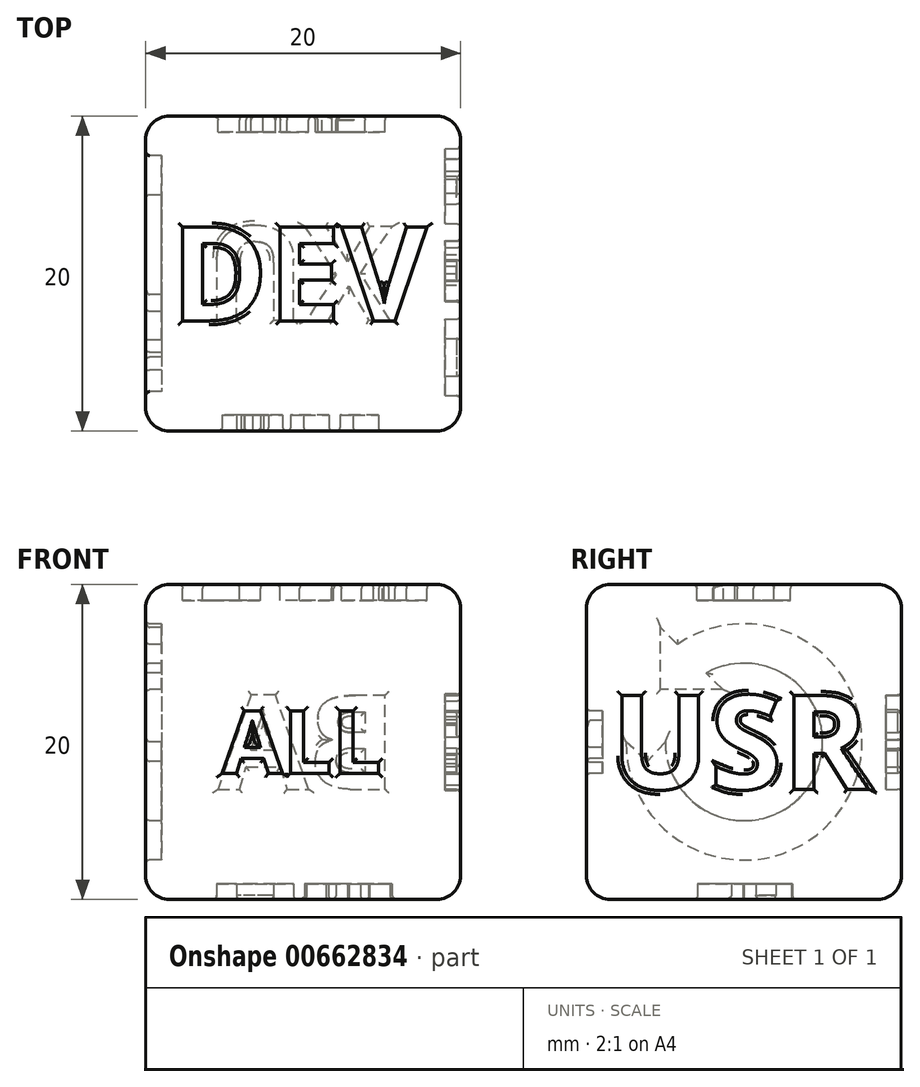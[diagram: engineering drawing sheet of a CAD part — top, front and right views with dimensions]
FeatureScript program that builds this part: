
annotation { "Feature Type Name" : "Feature", "Feature Type Description" : "" }
export const myFeature = defineFeature(function(context is Context, id is Id, definition is map)
    precondition{}
    {
        {
            assignVariable(context, id + "F0", {"name" : "textDepth", "anyValue" : 1});
        }
        {
            var Q0;
            Q0=qCreatedBy(makeId("Top.planeOp"),FACE);
            var sketch = newSketch(context, id + "F1", { "sketchPlane" : qUnion([Q0])});
            skLineSegment(sketch, "E0.bottom", {"start": v(0, 0) * mm, "end": v(20, 0) * mm});
            skLineSegment(sketch, "E0.top", {"start": v(0, 20) * mm, "end": v(20, 20) * mm});
            skLineSegment(sketch, "E0.left", {"start": v(0, 0) * mm, "end": v(0, 20) * mm});
            skLineSegment(sketch, "E0.right", {"start": v(20, 0) * mm, "end": v(20, 20) * mm});
            skSolve(sketch);
        }
        {
            var Q0;
            Q0 = qSketchRegion(id + "F1", true);
            extrude(context, id + "F2", {"entities" : qUnion([Q0]), "depth" : 20 * mm, "offsetDistance" : 25 * mm});
        }
        {
            var Q0;
            Q0=makeQuery(id+"F2.opExtrude","CAP_FACE",FACE,{"disambiguationData":[OSD([sQuery(id+"F1.wireOp",EDGE,"E0.bottom"),sQuery(id+"F1.wireOp",EDGE,"E0.top"),sQuery(id+"F1.wireOp",EDGE,"E0.left"),sQuery(id+"F1.wireOp",EDGE,"E0.right")])],"isStart":false});
            var Q1;
            Q1=makeQuery(id+"F2.opExtrude","SWEPT_FACE",FACE,{"disambiguationData":[OSD([sQuery(id+"F1.wireOp",EDGE,"E0.right")])]});
            var Q2;
            Q2=makeQuery(id+"F2.opExtrude","SWEPT_FACE",FACE,{"disambiguationData":[OSD([sQuery(id+"F1.wireOp",EDGE,"E0.bottom")])]});
            var Q3;
            Q3=makeQuery(id+"F2.opExtrude","CAP_FACE",FACE,{"disambiguationData":[OSD([sQuery(id+"F1.wireOp",EDGE,"E0.bottom"),sQuery(id+"F1.wireOp",EDGE,"E0.top"),sQuery(id+"F1.wireOp",EDGE,"E0.left"),sQuery(id+"F1.wireOp",EDGE,"E0.right")])],"isStart":true});
            var Q4;
            Q4=makeQuery(id+"F2.opExtrude","SWEPT_FACE",FACE,{"disambiguationData":[OSD([sQuery(id+"F1.wireOp",EDGE,"E0.top")])]});
            var Q5;
            Q5=makeQuery(id+"F2.opExtrude","SWEPT_FACE",FACE,{"disambiguationData":[OSD([sQuery(id+"F1.wireOp",EDGE,"E0.left")])]});
            fillet(context, id + "F3", {"entities" : qUnion([Q0, Q1, Q2, Q3, Q4, Q5]), "radius" : 1.5 * mm, "tangentPropagation" : true, "allowEdgeOverflow" : false});
        }
        {
            var Q0;
            Q0=makeQuery(id+"F2.opExtrude","CAP_FACE",FACE,{"disambiguationData":[OSD([sQuery(id+"F1.wireOp",EDGE,"E0.bottom"),sQuery(id+"F1.wireOp",EDGE,"E0.top"),sQuery(id+"F1.wireOp",EDGE,"E0.left"),sQuery(id+"F1.wireOp",EDGE,"E0.right")])],"isStart":false});
            var sketch = newSketch(context, id + "F4", { "sketchPlane" : qUnion([Q0])});
            skText(sketch, "E1", { "text": "DEV", "fontName": "OpenSans-Bold.ttf"});
            skLineSegment(sketch, "E2", {"start": v(10, 18.5) * mm, "end": v(10, 1.5) * mm, "construction": true});
            skLineSegment(sketch, "E3", {"start": v(1.6, 10) * mm, "end": v(18.4, 10) * mm, "construction": true});
            skLineSegment(sketch, "E4", {"start": v(1.5, 10) * mm, "end": v(18.5, 10) * mm, "construction": true});
            const initialGuessF4  = {"E1": [0.0016, 0.007, 1, 0, 0.006]};
            skSetInitialGuess(sketch, initialGuessF4);
            skSolve(sketch);
        }
        {
            var Q0;
            Q0 = qSketchRegion(id + "F4", true);
            extrude(context, id + "F5", {"entities" : qUnion([Q0]), "operationType" : NewBodyOperationType.REMOVE, "oppositeDirection" : true, "depth" : (getVariable(context, 'textDepth')) * mm, "offsetDistance" : 25 * mm});
        }
        {
            var Q0;
            Q0=makeQuery(id+"F2.opExtrude","SWEPT_FACE",FACE,{"disambiguationData":[OSD([sQuery(id+"F1.wireOp",EDGE,"E0.bottom")])]});
            var sketch = newSketch(context, id + "F6", { "sketchPlane" : qUnion([Q0])});
            skLineSegment(sketch, "E5", {"start": v(1.5, 10) * mm, "end": v(18.5, 10) * mm, "construction": true});
            skLineSegment(sketch, "E6", {"start": v(10, 18.5) * mm, "end": v(10, 1.5) * mm, "construction": true});
            skText(sketch, "E7", { "text": "ALL", "fontName": "OpenSans-Bold.ttf"});
            skLineSegment(sketch, "E8", {"start": v(2.29, 10) * mm, "end": v(17.71, 10) * mm, "construction": true});
            const initialGuessF6  = {"E7": [0.00486, 0.008, 1, 0, 0.004]};
            skSetInitialGuess(sketch, initialGuessF6);
            skSolve(sketch);
        }
        {
            var Q0;
            Q0 = qSketchRegion(id + "F6", true);
            extrude(context, id + "F7", {"entities" : qUnion([Q0]), "operationType" : NewBodyOperationType.REMOVE, "oppositeDirection" : true, "depth" : (getVariable(context, 'textDepth')) * mm, "offsetDistance" : 25 * mm});
        }
        {
            var Q0;
            Q0=makeQuery(id+"F2.opExtrude","SWEPT_FACE",FACE,{"disambiguationData":[OSD([sQuery(id+"F1.wireOp",EDGE,"E0.right")])]});
            var sketch = newSketch(context, id + "F8", { "sketchPlane" : qUnion([Q0])});
            skLineSegment(sketch, "E9", {"start": v(1.5, 10) * mm, "end": v(18.5, 10) * mm, "construction": true});
            skLineSegment(sketch, "E10", {"start": v(10, 18.5) * mm, "end": v(10, 1.5) * mm, "construction": true});
            skText(sketch, "E11", { "text": "USR", "fontName": "OpenSans-Bold.ttf"});
            skLineSegment(sketch, "E12", {"start": v(1.53, 10) * mm, "end": v(18.47, 10) * mm, "construction": true});
            const initialGuessF8  = {"E11": [0.00153, 0.007, 1, 0, 0.006]};
            skSetInitialGuess(sketch, initialGuessF8);
            skSolve(sketch);
        }
        {
            var Q0;
            Q0 = qSketchRegion(id + "F8", true);
            extrude(context, id + "F9", {"entities" : qUnion([Q0]), "operationType" : NewBodyOperationType.REMOVE, "oppositeDirection" : true, "depth" : (getVariable(context, 'textDepth')) * mm, "offsetDistance" : 25 * mm});
        }
        {
            var Q0;
            Q0=makeQuery(id+"F2.opExtrude","SWEPT_FACE",FACE,{"disambiguationData":[OSD([sQuery(id+"F1.wireOp",EDGE,"E0.top")])]});
            var sketch = newSketch(context, id + "F10", { "sketchPlane" : qUnion([Q0])});
            skLineSegment(sketch, "E13", {"start": v(-18.5, 10) * mm, "end": v(-1.5, 10) * mm, "construction": true});
            skLineSegment(sketch, "E14", {"start": v(-10, 18.5) * mm, "end": v(-10, 1.5) * mm, "construction": true});
            skText(sketch, "E15", { "text": "BA", "fontName": "OpenSans-Bold.ttf"});
            skLineSegment(sketch, "E16", {"start": v(-15.94, 10) * mm, "end": v(-4.06, 10) * mm, "construction": true});
            const initialGuessF10  = {"E15": [-0.01594, 0.007, 1, 0, 0.006]};
            skSetInitialGuess(sketch, initialGuessF10);
            skSolve(sketch);
        }
        {
            var Q0;
            Q0 = qSketchRegion(id + "F10", true);
            extrude(context, id + "F11", {"entities" : qUnion([Q0]), "operationType" : NewBodyOperationType.REMOVE, "oppositeDirection" : true, "depth" : (getVariable(context, 'textDepth')) * mm, "offsetDistance" : 25 * mm});
        }
        {
            var Q0;
            Q0=makeQuery(id+"F2.opExtrude","CAP_FACE",FACE,{"disambiguationData":[OSD([sQuery(id+"F1.wireOp",EDGE,"E0.bottom"),sQuery(id+"F1.wireOp",EDGE,"E0.top"),sQuery(id+"F1.wireOp",EDGE,"E0.left"),sQuery(id+"F1.wireOp",EDGE,"E0.right")])],"isStart":true});
            var sketch = newSketch(context, id + "F12", { "sketchPlane" : qUnion([Q0])});
            skLineSegment(sketch, "E17", {"start": v(18.5, -10) * mm, "end": v(1.5, -10) * mm, "construction": true});
            skLineSegment(sketch, "E18", {"start": v(10, -18.5) * mm, "end": v(10, -1.5) * mm, "construction": true});
            skText(sketch, "E19", { "text": "UX", "fontName": "OpenSans-Bold.ttf"});
            skLineSegment(sketch, "E20", {"start": v(16.2, -10) * mm, "end": v(3.8, -10) * mm, "construction": true});
            const initialGuessF12  = {"E19": [0.0038, -0.013, 1, 0, 0.006]};
            skSetInitialGuess(sketch, initialGuessF12);
            skSolve(sketch);
        }
        {
            var Q0;
            Q0 = qSketchRegion(id + "F12", true);
            extrude(context, id + "F13", {"entities" : qUnion([Q0]), "operationType" : NewBodyOperationType.REMOVE, "oppositeDirection" : true, "depth" : (getVariable(context, 'textDepth')) * mm, "offsetDistance" : 25 * mm});
        }
        {
            var Q0;
            Q0=makeQuery(id+"F2.opExtrude","SWEPT_FACE",FACE,{"disambiguationData":[OSD([sQuery(id+"F1.wireOp",EDGE,"E0.left")])]});
            var sketch = newSketch(context, id + "F14", { "sketchPlane" : qUnion([Q0])});
            skLineSegment(sketch, "E21", {"start": v(-18.5, 10) * mm, "end": v(-1.5, 10) * mm, "construction": true});
            skLineSegment(sketch, "E22", {"start": v(-10, 18.5) * mm, "end": v(-10, 1.5) * mm, "construction": true});
            skArc(sketch, "E23", {"start": v(-5.78, 16.2) * mm, "mid": v(-16.63, 6.5) * mm, "end": v(-2.5, 10) * mm});
            skArc(sketch, "E24", {"start": v(-7.6, 14.38) * mm, "mid": v(-14.3, 7.45) * mm, "end": v(-5, 10) * mm});
            skLineSegment(sketch, "E25", {"start": v(-8.65, 13.32) * mm, "end": v(-7.6, 14.38) * mm});
            skLineSegment(sketch, "E26", {"start": v(-8.65, 13.32) * mm, "end": v(-4.7, 13.32) * mm});
            skLineSegment(sketch, "E27", {"start": v(-4.7, 13.32) * mm, "end": v(-4.7, 17.27) * mm});
            skCircle(sketch, "E28", {"center": v(-10, 10) * mm, "radius": 6.25 * mm, "construction": true});
            skLineSegment(sketch, "E29", {"start": v(-4.7, 13.32) * mm, "end": v(-6.68, 15.3) * mm, "construction": true});
            skLineSegment(sketch, "E30", {"start": v(-10, 10) * mm, "end": v(-1.5, 18.5) * mm, "construction": true});
            skLineSegment(sketch, "E31", {"start": v(-5, 10) * mm, "end": v(-3.87, 8.77) * mm});
            skLineSegment(sketch, "E32", {"start": v(-3.87, 8.77) * mm, "end": v(-2.5, 10) * mm});
            skArc(sketch, "E33.trimOffspring", {"start": v(-4.7, 15.3) * mm, "mid": v(-4.7, 15.3) * mm, "end": v(-4.7, 15.31) * mm});
            skLineSegment(sketch, "E34.trimOffspring", {"start": v(-5.78, 16.2) * mm, "end": v(-4.7, 17.27) * mm});
            skSolve(sketch);
        }
        {
            var Q0;
            Q0 = qSketchRegion(id + "F14", true);
            extrude(context, id + "F15", {"entities" : qUnion([Q0]), "operationType" : NewBodyOperationType.REMOVE, "oppositeDirection" : true, "depth" : (getVariable(context, 'textDepth')) * mm, "offsetDistance" : 25 * mm});
        }
        {
            var Q0;
            Q0=makeQuery(id+"F2.opExtrude","SWEPT_FACE",FACE,{"disambiguationData":[OSD([sQuery(id+"F1.wireOp",EDGE,"E0.left")])]});
            var Q1;
            {var subQ1=sQuery(id+"F1.wireOp",EDGE,"E0.bottom");Q1=makeQuery(id+"F7.boolean.opBoolean","SPLIT",FACE,{"disambiguationData":[TD([makeQuery(id+"F7.opExtrude","SWEPT_FACE",FACE,{"disambiguationData":[OSD([sQuery(id+"F6.wireOp",EDGE,"E7.sketch_text.stroke-0")])]})])],"derivedFrom":makeQuery(id+"F2.opExtrude","SWEPT_FACE",FACE,{"disambiguationData":[OSD([subQ1])]})});}
            var Q2;
            Q2=makeQuery(id+"F7.boolean.opBoolean","SPLIT",FACE,{"disambiguationData":[TD([makeQuery(id+"F7.opExtrude","SWEPT_FACE",FACE,{"disambiguationData":[OSD([sQuery(id+"F6.wireOp",EDGE,"E7.sketch_text.stroke-8")])]})])],"derivedFrom":makeQuery(id+"F2.opExtrude","SWEPT_FACE",FACE,{"disambiguationData":[OSD([sQuery(id+"F1.wireOp",EDGE,"E0.bottom")])]})});
            var Q3;
            Q3=makeQuery(id+"F2.opExtrude","CAP_FACE",FACE,{"disambiguationData":[OSD([sQuery(id+"F1.wireOp",EDGE,"E0.bottom"),sQuery(id+"F1.wireOp",EDGE,"E0.top"),sQuery(id+"F1.wireOp",EDGE,"E0.left"),sQuery(id+"F1.wireOp",EDGE,"E0.right")])],"isStart":true});
            var Q4;
            {var subQ0=sQuery(id+"F1.wireOp",EDGE,"E0.left");var subQ1=sQuery(id+"F1.wireOp",EDGE,"E0.top");var subQ2=sQuery(id+"F1.wireOp",EDGE,"E0.right");var subQ3=sQuery(id+"F1.wireOp",EDGE,"E0.bottom");Q4=makeQuery(id+"F5.boolean.opBoolean","SPLIT",FACE,{"disambiguationData":[TD([makeQuery(id+"F5.opExtrude","SWEPT_FACE",FACE,{"disambiguationData":[OSD([sQuery(id+"F4.wireOp",EDGE,"E1.sketch_text.stroke-0")])]})])],"derivedFrom":makeQuery(id+"F2.opExtrude","CAP_FACE",FACE,{"disambiguationData":[OSD([subQ3,subQ1,subQ0,subQ2])],"isStart":false})});}
            var Q5;
            Q5=makeQuery(id+"F5.boolean.opBoolean","SPLIT",FACE,{"disambiguationData":[TD([makeQuery(id+"F5.opExtrude","SWEPT_FACE",FACE,{"disambiguationData":[OSD([sQuery(id+"F4.wireOp",EDGE,"E1.sketch_text.stroke-7")])]})])],"derivedFrom":makeQuery(id+"F2.opExtrude","CAP_FACE",FACE,{"disambiguationData":[OSD([sQuery(id+"F1.wireOp",EDGE,"E0.bottom"),sQuery(id+"F1.wireOp",EDGE,"E0.top"),sQuery(id+"F1.wireOp",EDGE,"E0.left"),sQuery(id+"F1.wireOp",EDGE,"E0.right")])],"isStart":false})});
            var Q6;
            {var subQ1=sQuery(id+"F1.wireOp",EDGE,"E0.top");Q6=makeQuery(id+"F11.boolean.opBoolean","SPLIT",FACE,{"disambiguationData":[TD([makeQuery(id+"F11.opExtrude","SWEPT_FACE",FACE,{"disambiguationData":[OSD([sQuery(id+"F10.wireOp",EDGE,"E15.sketch_text.stroke-0")])]})])],"derivedFrom":makeQuery(id+"F2.opExtrude","SWEPT_FACE",FACE,{"disambiguationData":[OSD([subQ1])]})});}
            var Q7;
            Q7=makeQuery(id+"F11.boolean.opBoolean","SPLIT",FACE,{"disambiguationData":[TD([makeQuery(id+"F11.opExtrude","SWEPT_FACE",FACE,{"disambiguationData":[OSD([sQuery(id+"F10.wireOp",EDGE,"E15.sketch_text.stroke-19")])]})])],"derivedFrom":makeQuery(id+"F2.opExtrude","SWEPT_FACE",FACE,{"disambiguationData":[OSD([sQuery(id+"F1.wireOp",EDGE,"E0.top")])]})});
            var Q8;
            Q8=makeQuery(id+"F11.boolean.opBoolean","SPLIT",FACE,{"disambiguationData":[TD([makeQuery(id+"F11.opExtrude","SWEPT_FACE",FACE,{"disambiguationData":[OSD([sQuery(id+"F10.wireOp",EDGE,"E15.sketch_text.stroke-12")])]})])],"derivedFrom":makeQuery(id+"F2.opExtrude","SWEPT_FACE",FACE,{"disambiguationData":[OSD([sQuery(id+"F1.wireOp",EDGE,"E0.top")])]})});
            var Q9;
            Q9=makeQuery(id+"F11.boolean.opBoolean","SPLIT",FACE,{"disambiguationData":[TD([makeQuery(id+"F11.opExtrude","SWEPT_FACE",FACE,{"disambiguationData":[OSD([sQuery(id+"F10.wireOp",EDGE,"E15.sketch_text.stroke-33")])]})])],"derivedFrom":makeQuery(id+"F2.opExtrude","SWEPT_FACE",FACE,{"disambiguationData":[OSD([sQuery(id+"F1.wireOp",EDGE,"E0.top")])]})});
            var Q10;
            {var subQ0=sQuery(id+"F1.wireOp",EDGE,"E0.right");Q10=makeQuery(id+"F9.boolean.opBoolean","SPLIT",FACE,{"disambiguationData":[TD([makeQuery(id+"F9.opExtrude","SWEPT_FACE",FACE,{"disambiguationData":[OSD([sQuery(id+"F8.wireOp",EDGE,"E11.sketch_text.stroke-0")])]})])],"derivedFrom":makeQuery(id+"F2.opExtrude","SWEPT_FACE",FACE,{"disambiguationData":[OSD([subQ0])]})});}
            var Q11;
            Q11=makeQuery(id+"F9.boolean.opBoolean","SPLIT",FACE,{"disambiguationData":[TD([makeQuery(id+"F9.opExtrude","SWEPT_FACE",FACE,{"disambiguationData":[OSD([sQuery(id+"F8.wireOp",EDGE,"E11.sketch_text.stroke-43")])]})])],"derivedFrom":makeQuery(id+"F2.opExtrude","SWEPT_FACE",FACE,{"disambiguationData":[OSD([sQuery(id+"F1.wireOp",EDGE,"E0.right")])]})});
            fillet(context, id + "F16", {"entities" : qUnion([Q0, Q1, Q2, Q3, Q4, Q5, Q6, Q7, Q8, Q9, Q10, Q11]), "radius" : 0.25 * mm, "tangentPropagation" : true, "allowEdgeOverflow" : false});
        }
    });
